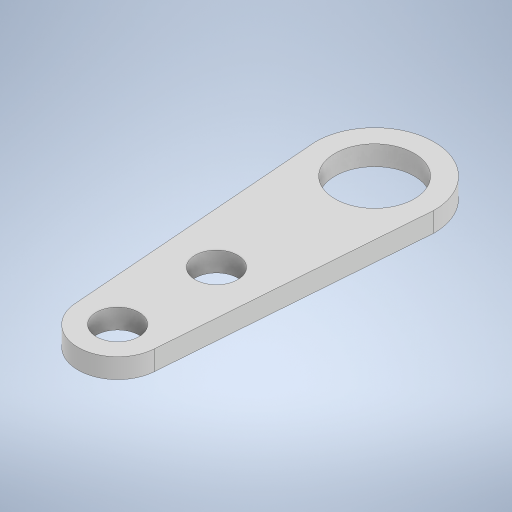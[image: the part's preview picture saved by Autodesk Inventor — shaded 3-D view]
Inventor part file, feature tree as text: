
AUTODESK INVENTOR PART (.ipt)
format: ipt  version: 2023 (Build 270158000, 158)  size: 246,784 bytes
history: native  units: mm
features: extrude x1, sketch x1
ambient origin geometry x8: Origin, YZ Plane, XZ Plane, XY Plane, X Axis, Y Axis, Z Axis, Center Point
bodies: Solid1 (feature_tree)
feature tree (2):
  extrude  "Extrusion1"  Depth=8.0mm
  sketch  "Sketch1"  dims[d0=6.0mm d1=8.0mm d2=2.15mm d3=5.0mm d4=2.15mm d5=4.0mm d6=4.0mm d7=1.0mm d8=0.0mm]
